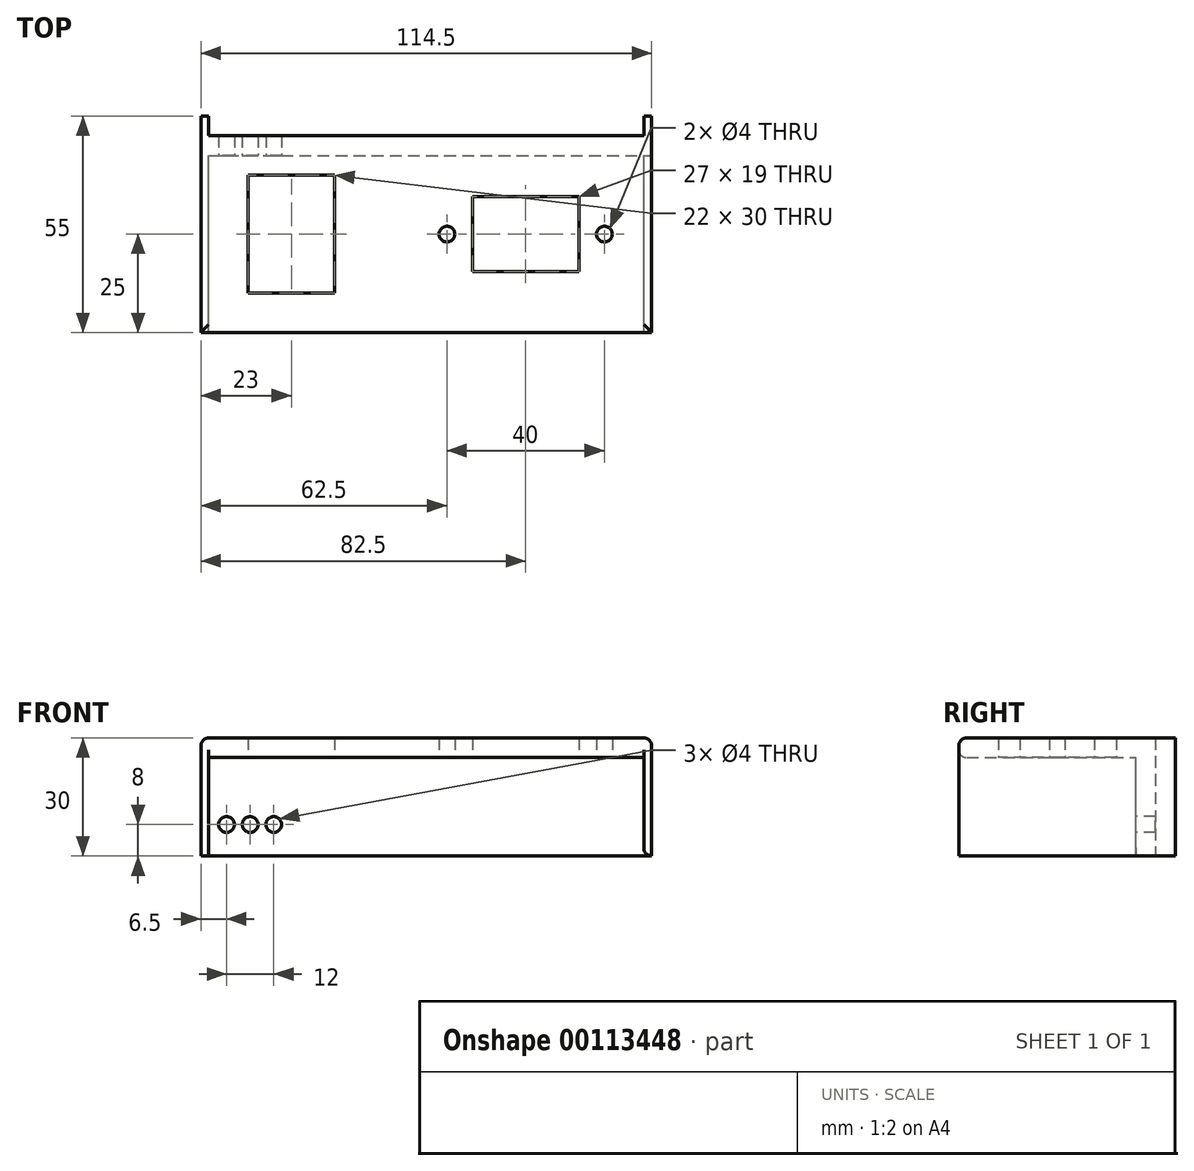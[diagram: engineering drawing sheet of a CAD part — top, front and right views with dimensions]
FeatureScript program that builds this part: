
annotation { "Feature Type Name" : "Feature", "Feature Type Description" : "" }
export const myFeature = defineFeature(function(context is Context, id is Id, definition is map)
    precondition{}
    {
        {
            var Q0;
            Q0=qCreatedBy(makeId("Top.planeOp"),FACE);
            var sketch = newSketch(context, id + "F0", { "sketchPlane" : qUnion([Q0])});
            skLineSegment(sketch, "E0.bottom", {"start": v(11, 15) * mm, "end": v(-11, 15) * mm});
            skLineSegment(sketch, "E0.top", {"start": v(11, -15) * mm, "end": v(-11, -15) * mm});
            skLineSegment(sketch, "E0.left", {"start": v(11, 15) * mm, "end": v(11, -15) * mm});
            skLineSegment(sketch, "E0.right", {"start": v(-11, 15) * mm, "end": v(-11, -15) * mm});
            skPoint(sketch, "E0.middle", {"position": v(0, 0) * mm});
            skLineSegment(sketch, "E1.bottom", {"start": v(89.5, -25) * mm, "end": v(-21, -25) * mm});
            skLineSegment(sketch, "E1.top", {"start": v(89.5, 25) * mm, "end": v(-21, 25) * mm});
            skLineSegment(sketch, "E1.left", {"start": v(89.5, -25) * mm, "end": v(89.5, 25) * mm});
            skLineSegment(sketch, "E1.right", {"start": v(-21, -25) * mm, "end": v(-21, 25) * mm});
            skPoint(sketch, "E1.middle", {"position": v(34.25, 0) * mm});
            skCircle(sketch, "E2", {"center": v(39.5, 0) * mm, "radius": 2 * mm});
            skCircle(sketch, "E3", {"center": v(79.5, 0) * mm, "radius": 2 * mm});
            skLineSegment(sketch, "E4.bottom", {"start": v(46, -9.5) * mm, "end": v(73, -9.5) * mm});
            skLineSegment(sketch, "E4.top", {"start": v(46, 9.5) * mm, "end": v(73, 9.5) * mm});
            skLineSegment(sketch, "E4.left", {"start": v(46, -9.5) * mm, "end": v(46, 9.5) * mm});
            skLineSegment(sketch, "E4.right", {"start": v(73, -9.5) * mm, "end": v(73, 9.5) * mm});
            skSolve(sketch);
        }
        {
            var Q0;
            Q0 = qSketchRegion(id + "F0", true);
            extrude(context, id + "F1", {"entities" : qUnion([Q0]), "depth" : 5 * mm});
        }
        {
            var Q0;
            Q0=makeQuery(id+"F1.opExtrude","CAP_FACE",FACE,{"disambiguationData":[OSD([sQuery(id+"F0.wireOp",EDGE,"E0.bottom"),sQuery(id+"F0.wireOp",EDGE,"E0.top"),sQuery(id+"F0.wireOp",EDGE,"E0.left"),sQuery(id+"F0.wireOp",EDGE,"E0.right"),sQuery(id+"F0.wireOp",EDGE,"E1.bottom"),sQuery(id+"F0.wireOp",EDGE,"E1.top"),sQuery(id+"F0.wireOp",EDGE,"E1.left"),sQuery(id+"F0.wireOp",EDGE,"E1.right"),sQuery(id+"F0.wireOp",EDGE,"E2"),sQuery(id+"F0.wireOp",EDGE,"E3"),sQuery(id+"F0.wireOp",EDGE,"E4.bottom"),sQuery(id+"F0.wireOp",EDGE,"E4.top"),sQuery(id+"F0.wireOp",EDGE,"E4.left"),sQuery(id+"F0.wireOp",EDGE,"E4.right")])],"isStart":true});
            var sketch = newSketch(context, id + "F2", { "sketchPlane" : qUnion([Q0])});
            skLineSegment(sketch, "E5.bottom", {"start": v(-21, -25) * mm, "end": v(89.5, -25) * mm});
            skLineSegment(sketch, "E5.top", {"start": v(-21, -20) * mm, "end": v(89.5, -20) * mm});
            skLineSegment(sketch, "E5.left", {"start": v(-21, -25) * mm, "end": v(-21, -20) * mm});
            skLineSegment(sketch, "E5.right", {"start": v(89.5, -25) * mm, "end": v(89.5, -20) * mm});
            skSolve(sketch);
        }
        {
            var Q0;
            Q0 = qSketchRegion(id + "F2", true);
            extrude(context, id + "F3", {"entities" : qUnion([Q0]), "operationType" : NewBodyOperationType.ADD, "depth" : 25 * mm});
        }
        {
            var Q0;
            Q0=makeQuery(id+"F3.opExtrude","SWEPT_FACE",FACE,{"disambiguationData":[OSD([sQuery(id+"F2.wireOp",EDGE,"E5.top")])]});
            var sketch = newSketch(context, id + "F4", { "sketchPlane" : qUnion([Q0])});
            skCircle(sketch, "E6", {"center": v(-16.5, -17) * mm, "radius": 2 * mm});
            skCircle(sketch, "E7.1.0.0", {"center": v(-10.5, -17) * mm, "radius": 2 * mm});
            skLineSegment(sketch, "E7.direction1", {"start": v(-16.5, -17) * mm, "end": v(-10.5, -17) * mm, "construction": true});
            skCircle(sketch, "E8.0.2.0", {"center": v(-4.5, -17) * mm, "radius": 2 * mm});
            skSolve(sketch);
        }
        {
            var Q0;
            Q0 = qSketchRegion(id + "F4", true);
            extrude(context, id + "F5", {"entities" : qUnion([Q0]), "operationType" : NewBodyOperationType.REMOVE, "endBound" : BoundingType.THROUGH_ALL, "oppositeDirection" : true, "depth" : 25 * mm});
        }
        {
            var Q0;
            Q0=makeQuery(id+"F3.boolean.opBoolean","MERGE",FACE,{"derivedFrom":[makeQuery(id+"F1.opExtrude","SWEPT_FACE",FACE,{"disambiguationData":[OSD([sQuery(id+"F0.wireOp",EDGE,"E1.top")])]}),makeQuery(id+"F3.opExtrude","SWEPT_FACE",FACE,{"disambiguationData":[OSD([sQuery(id+"F2.wireOp",EDGE,"E5.bottom")])]})]});
            var sketch = newSketch(context, id + "F6", { "sketchPlane" : qUnion([Q0])});
            skLineSegment(sketch, "E9.bottom", {"start": v(21, 5) * mm, "end": v(23, 5) * mm});
            skLineSegment(sketch, "E9.top", {"start": v(21, -25) * mm, "end": v(23, -25) * mm});
            skLineSegment(sketch, "E9.left", {"start": v(21, 5) * mm, "end": v(21, -25) * mm});
            skLineSegment(sketch, "E9.right", {"start": v(23, 5) * mm, "end": v(23, -25) * mm});
            skLineSegment(sketch, "E10.bottom", {"start": v(-89.5, -25) * mm, "end": v(-91.5, -25) * mm});
            skLineSegment(sketch, "E10.top", {"start": v(-89.5, 5) * mm, "end": v(-91.5, 5) * mm});
            skLineSegment(sketch, "E10.left", {"start": v(-89.5, -25) * mm, "end": v(-89.5, 5) * mm});
            skLineSegment(sketch, "E10.right", {"start": v(-91.5, -25) * mm, "end": v(-91.5, 5) * mm});
            skSolve(sketch);
        }
        {
            var Q0;
            Q0 = qSketchRegion(id + "F6", true);
            var Q1;
            Q1=makeQuery(id+"F1.opExtrude","SWEPT_FACE",FACE,{"disambiguationData":[OSD([sQuery(id+"F0.wireOp",EDGE,"E1.bottom")])]});
            extrude(context, id + "F7", {"entities" : qUnion([Q0]), "operationType" : NewBodyOperationType.ADD, "endBound" : BoundingType.UP_TO_SURFACE, "oppositeDirection" : true, "endBoundEntityFace" : qUnion([Q1]), "depth" : 25 * mm});
        }
        {
            var Q0;
            Q0 = qSketchRegion(id + "F6", true);
            extrude(context, id + "F8", {"entities" : qUnion([Q0]), "operationType" : NewBodyOperationType.ADD, "depth" : 5 * mm});
        }
        {
            var Q0;
            Q0=makeQuery(id+"F3.opExtrude","SWEPT_EDGE",EDGE,{"disambiguationData":[OSD([sQuery(id+"F0.wireOp",EDGE,"E1.left"),sQuery(id+"F2.wireOp",EDGE,"E5.top"),sQuery(id+"F2.wireOp",EDGE,"E5.right")])]});
            var Q1;
            Q1=makeQuery(id+"F3.opExtrude","CAP_EDGE",EDGE,{"disambiguationData":[OSD([sQuery(id+"F2.wireOp",EDGE,"E5.top")])],"isStart":true});
            var Q2;
            Q2=makeQuery(id+"F1.opExtrude","CAP_EDGE",EDGE,{"disambiguationData":[OSD([sQuery(id+"F0.wireOp",EDGE,"E1.left")])],"isStart":true});
            var Q3;
            Q3=makeQuery(id+"F1.opExtrude","CAP_EDGE",EDGE,{"disambiguationData":[OSD([sQuery(id+"F0.wireOp",EDGE,"E1.bottom")])],"isStart":true});
            var Q4;
            {var subQ0=sQuery(id+"F0.wireOp",EDGE,"E1.bottom");var subQ1=makeQuery(id+"F1.opExtrude","SWEPT_FACE",FACE,{"disambiguationData":[OSD([subQ0])]});Q4=makeQuery(id+"F7.boolean.opBoolean","MERGE",EDGE,{"derivedFrom":[makeQuery(id+"F1.opExtrude","CAP_EDGE",EDGE,{"disambiguationData":[OSD([subQ0])],"isStart":false}),makeQuery(id+"F7.opExtrude","TWEAK_EDGE",EDGE,{"derivedFrom":[subQ1,makeQuery(id+"F6.imprint","IMPRINT",EDGE,{"derivedFrom":sQuery(id+"F6.wireOp",EDGE,"E9.bottom")})]}),makeQuery(id+"F7.opExtrude","TWEAK_EDGE",EDGE,{"derivedFrom":[subQ1,makeQuery(id+"F6.imprint","IMPRINT",EDGE,{"derivedFrom":sQuery(id+"F6.wireOp",EDGE,"E10.top")})]})]});}
            var Q5;
            Q5=makeQuery(id+"F7.opExtrude","SWEPT_EDGE",EDGE,{"disambiguationData":[OSD([sQuery(id+"F2.wireOp",EDGE,"E5.bottom"),sQuery(id+"F6.wireOp",EDGE,"E10.bottom"),sQuery(id+"F6.wireOp",EDGE,"E10.left")])]});
            var Q6;
            Q6=makeQuery(id+"F3.opExtrude","SWEPT_EDGE",EDGE,{"disambiguationData":[OSD([sQuery(id+"F0.wireOp",EDGE,"E1.right"),sQuery(id+"F2.wireOp",EDGE,"E5.top"),sQuery(id+"F2.wireOp",EDGE,"E5.left")])]});
            var Q7;
            Q7=makeQuery(id+"F1.opExtrude","CAP_EDGE",EDGE,{"disambiguationData":[OSD([sQuery(id+"F0.wireOp",EDGE,"E1.right")])],"isStart":true});
            var Q8;
            {var subQ0=sQuery(id+"F6.wireOp",EDGE,"E9.right");var subQ1=sQuery(id+"F6.wireOp",EDGE,"E9.bottom");Q8=makeQuery(id+"F8.boolean.opBoolean","MERGE",EDGE,{"derivedFrom":[makeQuery(id+"F7.opExtrude","SWEPT_EDGE",EDGE,{"disambiguationData":[OSD([subQ1,subQ0])]}),makeQuery(id+"F8.opExtrude","SWEPT_EDGE",EDGE,{"disambiguationData":[OSD([subQ1,subQ0])]})]});}
            var Q9;
            {var subQ0=sQuery(id+"F6.wireOp",EDGE,"E10.right");var subQ1=sQuery(id+"F6.wireOp",EDGE,"E10.top");Q9=makeQuery(id+"F8.boolean.opBoolean","MERGE",EDGE,{"derivedFrom":[makeQuery(id+"F7.opExtrude","SWEPT_EDGE",EDGE,{"disambiguationData":[OSD([subQ1,subQ0])]}),makeQuery(id+"F8.opExtrude","SWEPT_EDGE",EDGE,{"disambiguationData":[OSD([subQ1,subQ0])]})]});}
            fillet(context, id + "F9", {"entities" : qUnion([Q0, Q1, Q2, Q3, Q4, Q5, Q6, Q7, Q8, Q9]), "radius" : 2 * mm, "tangentPropagation" : true, "allowEdgeOverflow" : false});
        }
    });
